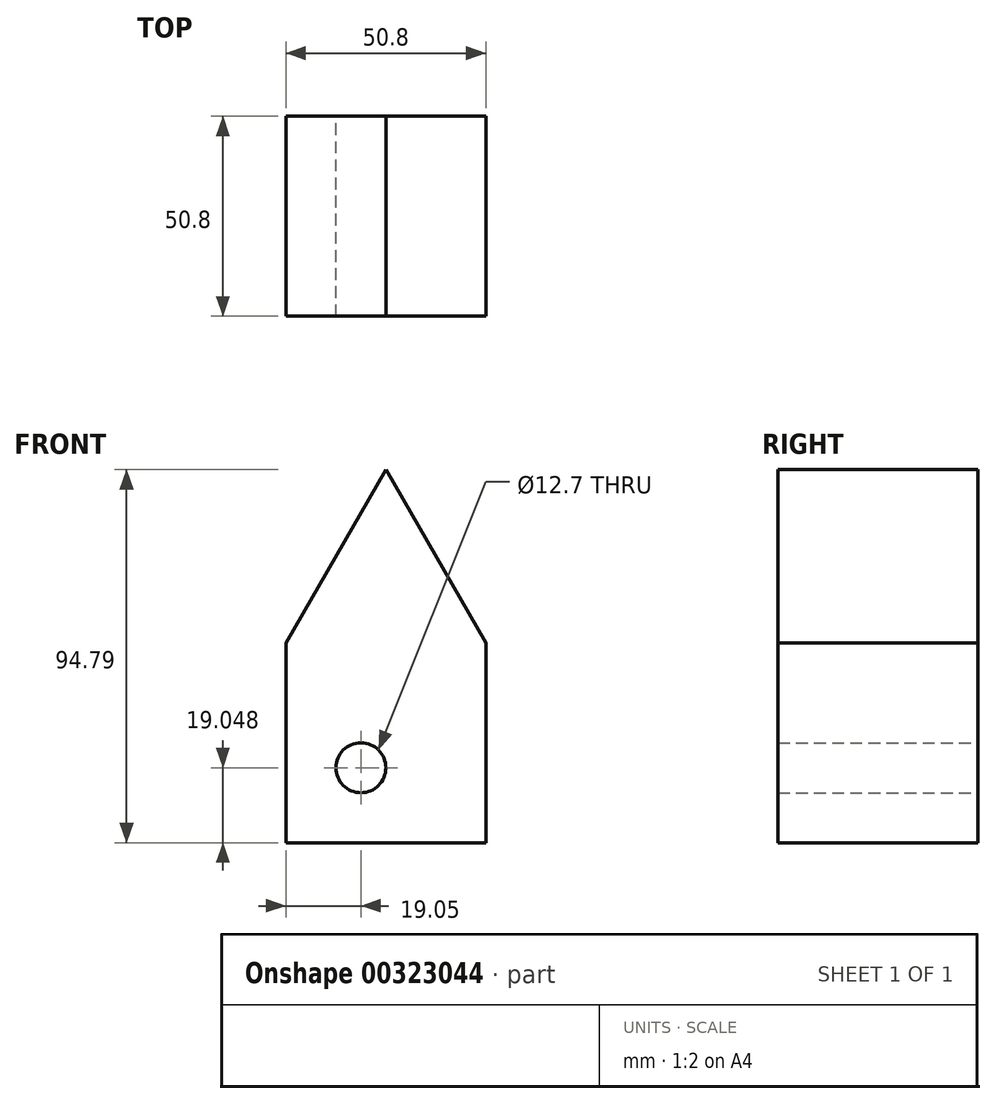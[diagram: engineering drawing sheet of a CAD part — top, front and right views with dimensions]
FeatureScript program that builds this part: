
annotation { "Feature Type Name" : "Feature", "Feature Type Description" : "" }
export const myFeature = defineFeature(function(context is Context, id is Id, definition is map)
    precondition{}
    {
        {
            var Q0;
            Q0=qCreatedBy(makeId("Front.planeOp"),FACE);
            var sketch = newSketch(context, id + "F0", { "sketchPlane" : qUnion([Q0])});
            skLineSegment(sketch, "E0.left", {"start": v(0, 0) * mm, "end": v(0, 8.18) * mm});
            skLineSegment(sketch, "E0.right", {"start": v(-25.4, 0) * mm, "end": v(-25.4, 8.18) * mm});
            skLineSegment(sketch, "E1.top", {"start": v(-25.4, -42.62) * mm, "end": v(25.4, -42.62) * mm});
            skLineSegment(sketch, "E1.left", {"start": v(-25.4, 8.18) * mm, "end": v(-25.4, -42.62) * mm});
            skLineSegment(sketch, "E1.right", {"start": v(25.4, 8.18) * mm, "end": v(25.4, -42.62) * mm});
            skLineSegment(sketch, "E2.bottom", {"start": v(25.4, -42.62) * mm, "end": v(25.4, -42.62) * mm});
            skLineSegment(sketch, "E2.top", {"start": v(25.4, 0) * mm, "end": v(25.4, 0) * mm});
            skLineSegment(sketch, "E2.left", {"start": v(25.4, -42.62) * mm, "end": v(25.4, 0) * mm});
            skLineSegment(sketch, "E2.right", {"start": v(25.4, -42.62) * mm, "end": v(25.4, 0) * mm});
            skLineSegment(sketch, "E3", {"start": v(-25.4, 8.18) * mm, "end": v(0, 52.17) * mm});
            skLineSegment(sketch, "E4", {"start": v(0, 52.17) * mm, "end": v(25.4, 8.18) * mm});
            skCircle(sketch, "E5", {"center": v(-6.35, -23.57) * mm, "radius": 6.35 * mm});
            skSolve(sketch);
        }
        {
            var Q0;
            Q0 = qSketchRegion(id + "F0", true);
            extrude(context, id + "F1", {"entities" : qUnion([Q0]), "depth" : 50.8 * mm});
        }
    });
